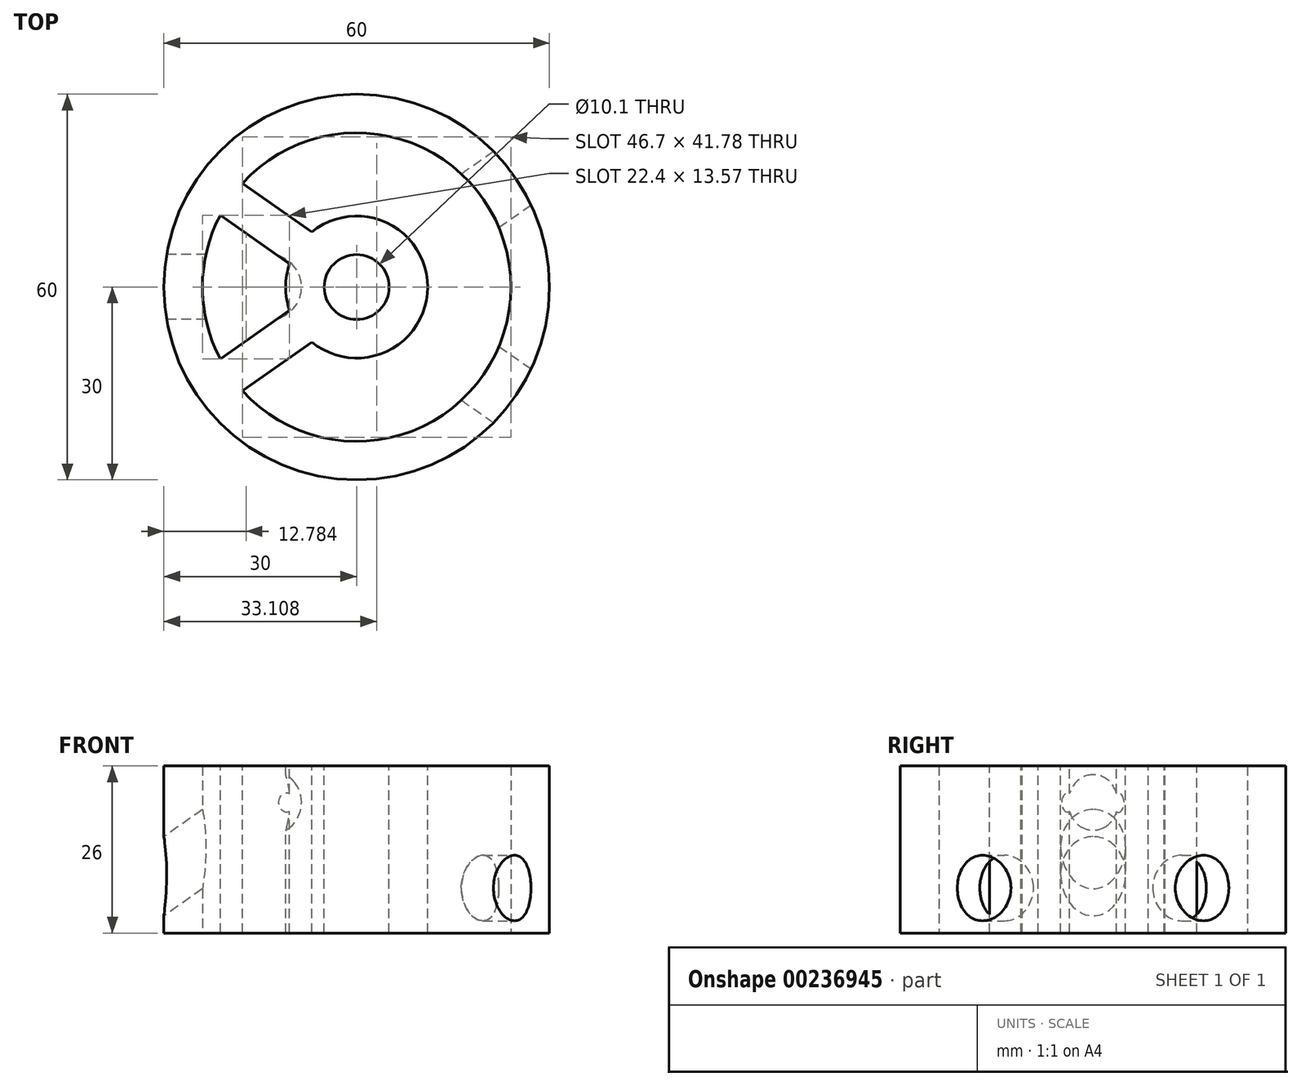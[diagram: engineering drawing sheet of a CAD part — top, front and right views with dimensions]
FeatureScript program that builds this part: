
annotation { "Feature Type Name" : "Feature", "Feature Type Description" : "" }
export const myFeature = defineFeature(function(context is Context, id is Id, definition is map)
    precondition{}
    {
        {
            var Q0;
            Q0=qCreatedBy(makeId("Top.planeOp"),FACE);
            var sketch = newSketch(context, id + "F0", { "sketchPlane" : qUnion([Q0])});
            skCircle(sketch, "E0", {"center": v(0, 0) * mm, "radius": 30 * mm});
            skCircle(sketch, "E1", {"center": v(0, 0) * mm, "radius": 24 * mm});
            skSolve(sketch);
        }
        {
            var Q0;
            Q0 = qSketchRegion(id + "F0", true);
            extrude(context, id + "F1", {"entities" : qUnion([Q0]), "depth" : 26 * mm});
        }
        {
            var Q0;
            Q0=makeQuery(id+"F1.opExtrude","CAP_FACE",FACE,{"disambiguationData":[OSD([sQuery(id+"F0.wireOp",EDGE,"E0"),sQuery(id+"F0.wireOp",EDGE,"E1")])],"isStart":false});
            var sketch = newSketch(context, id + "F2", { "sketchPlane" : qUnion([Q0])});
            skCircle(sketch, "E2", {"center": v(0, 0) * mm, "radius": 5.05 * mm});
            skCircle(sketch, "E3", {"center": v(0, 0) * mm, "radius": 11.05 * mm});
            skLineSegment(sketch, "E4", {"start": v(0, 0) * mm, "end": v(-19.66, 13.77) * mm});
            skLineSegment(sketch, "E5", {"start": v(0, 0) * mm, "end": v(-19.66, -13.77) * mm});
            skLineSegment(sketch, "E6", {"start": v(0, 0) * mm, "end": v(19.66, -13.77) * mm});
            skLineSegment(sketch, "E7", {"start": v(0, 0) * mm, "end": v(19.66, 13.77) * mm});
            skLineSegment(sketch, "E8.0", {"start": v(-1.72, 2.46) * mm, "end": v(-21.38, -11.3) * mm});
            skLineSegment(sketch, "E8.1", {"start": v(-1.72, 2.46) * mm, "end": v(17.94, 16.22) * mm});
            skLineSegment(sketch, "E9.0", {"start": v(1.72, -2.46) * mm, "end": v(-17.94, -16.22) * mm});
            skLineSegment(sketch, "E9.1", {"start": v(1.72, -2.46) * mm, "end": v(21.38, 11.3) * mm});
            skCircle(sketch, "E10", {"center": v(0, 0) * mm, "radius": 24 * mm});
            skLineSegment(sketch, "E11.0", {"start": v(1.72, 2.46) * mm, "end": v(-17.94, 16.22) * mm});
            skLineSegment(sketch, "E11.1", {"start": v(1.72, 2.46) * mm, "end": v(21.38, -11.3) * mm});
            skLineSegment(sketch, "E12.0", {"start": v(-1.72, -2.46) * mm, "end": v(-21.38, 11.3) * mm});
            skLineSegment(sketch, "E12.1", {"start": v(-1.72, -2.46) * mm, "end": v(17.94, -16.22) * mm});
            skSolve(sketch);
        }
        {
            var Q0;
            {var subQ0=sQuery(id+"F2.wireOp",EDGE,"E4");var subQ1=sQuery(id+"F2.wireOp",EDGE,"E3");var subQ2=makeQuery(id+"F2.imprint","INTERSECT",VERTEX,{"derivedFrom":[subQ1,subQ0]});Q0=makeQuery(id+"F2.imprint","IMPRINT",FACE,{"disambiguationData":[TD([[makeQuery(id+"F2.imprint","IMPRINT",EDGE,{"disambiguationData":[TD([[subQ2,-1.0]])],"derivedFrom":subQ1}),-1.0]])]});}
            var Q1;
            {var subQ0=sQuery(id+"F2.wireOp",EDGE,"E11.0");var subQ1=sQuery(id+"F2.wireOp",EDGE,"E3");var subQ2=makeQuery(id+"F2.imprint","INTERSECT",VERTEX,{"derivedFrom":[subQ1,subQ0]});Q1=makeQuery(id+"F2.imprint","IMPRINT",FACE,{"disambiguationData":[TD([[makeQuery(id+"F2.imprint","IMPRINT",EDGE,{"disambiguationData":[TD([[subQ2,-1.0]])],"derivedFrom":subQ1}),-1.0]])]});}
            var Q2;
            {var subQ0=sQuery(id+"F2.wireOp",EDGE,"E11.0");var subQ1=sQuery(id+"F2.wireOp",EDGE,"E2");var subQ2=makeQuery(id+"F2.imprint","INTERSECT",VERTEX,{"derivedFrom":[subQ1,subQ0]});Q2=makeQuery(id+"F2.imprint","IMPRINT",FACE,{"disambiguationData":[TD([[makeQuery(id+"F2.imprint","IMPRINT",EDGE,{"disambiguationData":[TD([[subQ2,-1.0]])],"derivedFrom":subQ1}),-1.0]])]});}
            var Q3;
            {var subQ0=sQuery(id+"F2.wireOp",EDGE,"E4");var subQ1=sQuery(id+"F2.wireOp",EDGE,"E2");var subQ2=makeQuery(id+"F2.imprint","INTERSECT",VERTEX,{"derivedFrom":[subQ1,subQ0]});Q3=makeQuery(id+"F2.imprint","IMPRINT",FACE,{"disambiguationData":[TD([[makeQuery(id+"F2.imprint","IMPRINT",EDGE,{"disambiguationData":[TD([[subQ2,-1.0]])],"derivedFrom":subQ1}),-1.0]])]});}
            var Q4;
            {var subQ0=sQuery(id+"F2.wireOp",EDGE,"E12.0");var subQ1=sQuery(id+"F2.wireOp",EDGE,"E3");var subQ2=makeQuery(id+"F2.imprint","INTERSECT",VERTEX,{"derivedFrom":[subQ1,subQ0]});Q4=makeQuery(id+"F2.imprint","IMPRINT",FACE,{"disambiguationData":[TD([[makeQuery(id+"F2.imprint","IMPRINT",EDGE,{"disambiguationData":[TD([[subQ2,-1.0]])],"derivedFrom":subQ1}),1.0]])]});}
            var Q5;
            {var subQ5=sQuery(id+"F2.wireOp",EDGE,"E12.0");var subQ6=sQuery(id+"F2.wireOp",EDGE,"E2");var subQ7=makeQuery(id+"F2.imprint","INTERSECT",VERTEX,{"derivedFrom":[subQ6,subQ5]});Q5=makeQuery(id+"F2.imprint","IMPRINT",FACE,{"disambiguationData":[TD([[makeQuery(id+"F2.imprint","IMPRINT",EDGE,{"disambiguationData":[TD([[subQ7,-1.0]])],"derivedFrom":subQ6}),-1.0]])]});}
            var Q6;
            {var subQ0=sQuery(id+"F2.wireOp",EDGE,"E5");var subQ1=sQuery(id+"F2.wireOp",EDGE,"E2");var subQ2=makeQuery(id+"F2.imprint","INTERSECT",VERTEX,{"derivedFrom":[subQ1,subQ0]});Q6=makeQuery(id+"F2.imprint","IMPRINT",FACE,{"disambiguationData":[TD([[makeQuery(id+"F2.imprint","IMPRINT",EDGE,{"disambiguationData":[TD([[subQ2,-1.0]])],"derivedFrom":subQ1}),-1.0]])]});}
            var Q7;
            {var subQ0=sQuery(id+"F2.wireOp",EDGE,"E9.0");var subQ1=sQuery(id+"F2.wireOp",EDGE,"E2");var subQ2=makeQuery(id+"F2.imprint","INTERSECT",VERTEX,{"derivedFrom":[subQ1,subQ0]});Q7=makeQuery(id+"F2.imprint","IMPRINT",FACE,{"disambiguationData":[TD([[makeQuery(id+"F2.imprint","IMPRINT",EDGE,{"disambiguationData":[TD([[subQ2,-1.0]])],"derivedFrom":subQ1}),-1.0]])]});}
            var Q8;
            {var subQ0=sQuery(id+"F2.wireOp",EDGE,"E12.1");var subQ1=sQuery(id+"F2.wireOp",EDGE,"E2");var subQ2=makeQuery(id+"F2.imprint","INTERSECT",VERTEX,{"derivedFrom":[subQ1,subQ0]});Q8=makeQuery(id+"F2.imprint","IMPRINT",FACE,{"disambiguationData":[TD([[makeQuery(id+"F2.imprint","IMPRINT",EDGE,{"disambiguationData":[TD([[subQ2,-1.0]])],"derivedFrom":subQ1}),-1.0]])]});}
            var Q9;
            {var subQ1=sQuery(id+"F2.wireOp",EDGE,"E2");var subQ5=sQuery(id+"F2.wireOp",EDGE,"E6");var subQ6=makeQuery(id+"F2.imprint","INTERSECT",VERTEX,{"derivedFrom":[subQ1,subQ5]});Q9=makeQuery(id+"F2.imprint","IMPRINT",FACE,{"disambiguationData":[TD([[makeQuery(id+"F2.imprint","IMPRINT",EDGE,{"disambiguationData":[TD([[subQ6,-1.0]])],"derivedFrom":subQ1}),-1.0]])]});}
            var Q10;
            {var subQ0=sQuery(id+"F2.wireOp",EDGE,"E9.1");var subQ1=sQuery(id+"F2.wireOp",EDGE,"E3");var subQ2=makeQuery(id+"F2.imprint","INTERSECT",VERTEX,{"derivedFrom":[subQ1,subQ0]});Q10=makeQuery(id+"F2.imprint","IMPRINT",FACE,{"disambiguationData":[TD([[makeQuery(id+"F2.imprint","IMPRINT",EDGE,{"disambiguationData":[TD([[subQ2,1.0]])],"derivedFrom":subQ1}),1.0]])]});}
            var Q11;
            {var subQ0=sQuery(id+"F2.wireOp",EDGE,"E7");var subQ1=sQuery(id+"F2.wireOp",EDGE,"E2");var subQ2=makeQuery(id+"F2.imprint","INTERSECT",VERTEX,{"derivedFrom":[subQ1,subQ0]});Q11=makeQuery(id+"F2.imprint","IMPRINT",FACE,{"disambiguationData":[TD([[makeQuery(id+"F2.imprint","IMPRINT",EDGE,{"disambiguationData":[TD([[subQ2,1.0]])],"derivedFrom":subQ1}),-1.0]])]});}
            var Q12;
            {var subQ0=sQuery(id+"F2.wireOp",EDGE,"E7");var subQ1=sQuery(id+"F2.wireOp",EDGE,"E2");var subQ2=makeQuery(id+"F2.imprint","INTERSECT",VERTEX,{"derivedFrom":[subQ1,subQ0]});Q12=makeQuery(id+"F2.imprint","IMPRINT",FACE,{"disambiguationData":[TD([[makeQuery(id+"F2.imprint","IMPRINT",EDGE,{"disambiguationData":[TD([[subQ2,-1.0]])],"derivedFrom":subQ1}),-1.0]])]});}
            var Q13;
            {var subQ0=sQuery(id+"F2.wireOp",EDGE,"E8.1");var subQ1=sQuery(id+"F2.wireOp",EDGE,"E2");var subQ2=makeQuery(id+"F2.imprint","INTERSECT",VERTEX,{"derivedFrom":[subQ1,subQ0]});Q13=makeQuery(id+"F2.imprint","IMPRINT",FACE,{"disambiguationData":[TD([[makeQuery(id+"F2.imprint","IMPRINT",EDGE,{"disambiguationData":[TD([[subQ2,-1.0]])],"derivedFrom":subQ1}),-1.0]])]});}
            var Q14;
            {var subQ0=sQuery(id+"F2.wireOp",EDGE,"E8.0");var subQ1=sQuery(id+"F2.wireOp",EDGE,"E2");var subQ2=makeQuery(id+"F2.imprint","INTERSECT",VERTEX,{"derivedFrom":[subQ1,subQ0]});Q14=makeQuery(id+"F2.imprint","IMPRINT",FACE,{"disambiguationData":[TD([[makeQuery(id+"F2.imprint","IMPRINT",EDGE,{"disambiguationData":[TD([[subQ2,-1.0]])],"derivedFrom":subQ1}),-1.0]])]});}
            var Q15;
            {var subQ0=sQuery(id+"F2.wireOp",EDGE,"E11.1");var subQ1=sQuery(id+"F2.wireOp",EDGE,"E2");var subQ2=makeQuery(id+"F2.imprint","INTERSECT",VERTEX,{"derivedFrom":[subQ1,subQ0]});Q15=makeQuery(id+"F2.imprint","IMPRINT",FACE,{"disambiguationData":[TD([[makeQuery(id+"F2.imprint","IMPRINT",EDGE,{"disambiguationData":[TD([[subQ2,1.0]])],"derivedFrom":subQ1}),-1.0]])]});}
            var Q16;
            {var subQ0=sQuery(id+"F2.wireOp",EDGE,"E8.0");var subQ1=sQuery(id+"F2.wireOp",EDGE,"E3");var subQ2=makeQuery(id+"F2.imprint","INTERSECT",VERTEX,{"derivedFrom":[subQ1,subQ0]});Q16=makeQuery(id+"F2.imprint","IMPRINT",FACE,{"disambiguationData":[TD([[makeQuery(id+"F2.imprint","IMPRINT",EDGE,{"disambiguationData":[TD([[subQ2,-1.0]])],"derivedFrom":subQ1}),-1.0]])]});}
            var Q17;
            {var subQ0=sQuery(id+"F2.wireOp",EDGE,"E5");var subQ1=sQuery(id+"F2.wireOp",EDGE,"E3");var subQ2=makeQuery(id+"F2.imprint","INTERSECT",VERTEX,{"derivedFrom":[subQ1,subQ0]});Q17=makeQuery(id+"F2.imprint","IMPRINT",FACE,{"disambiguationData":[TD([[makeQuery(id+"F2.imprint","IMPRINT",EDGE,{"disambiguationData":[TD([[subQ2,-1.0]])],"derivedFrom":subQ1}),-1.0]])]});}
            extrude(context, id + "F3", {"entities" : qUnion([Q0, Q1, Q2, Q3, Q4, Q5, Q6, Q7, Q8, Q9, Q10, Q11, Q12, Q13, Q14, Q15, Q16, Q17]), "operationType" : NewBodyOperationType.ADD, "oppositeDirection" : true, "depth" : 26 * mm});
        }
        {
            var Q0;
            Q0=qCreatedBy(makeId("Front.planeOp"),FACE);
            var sketch = newSketch(context, id + "F4", { "sketchPlane" : qUnion([Q0])});
            skLineSegment(sketch, "E13", {"start": v(-30, 0) * mm, "end": v(-30, 28) * mm});
            skLineSegment(sketch, "E14", {"start": v(30, 28) * mm, "end": v(30, 0) * mm});
            skLineSegment(sketch, "E15.0", {"start": v(-30, 0) * mm, "end": v(30, 0) * mm});
            skLineSegment(sketch, "E16", {"start": v(-30, 15) * mm, "end": v(-16.52, 24.44) * mm});
            skLineSegment(sketch, "E17", {"start": v(-9.5, 23.2) * mm, "end": v(-9.5, 23.2) * mm});
            skLineSegment(sketch, "E18", {"start": v(-10.73, 16.16) * mm, "end": v(-35.94, -1.5) * mm});
            skLineSegment(sketch, "E19", {"start": v(-35.94, -1.5) * mm, "end": v(-41.73, 6.78) * mm});
            skLineSegment(sketch, "E20", {"start": v(-30, 15) * mm, "end": v(-41.73, 6.78) * mm});
            skPoint(sketch, "E21.visualSharp", {"position": v(-6.6, 19.06) * mm});
            skArc(sketch, "E21.filletArc", {"start": v(-10.73, 16.16) * mm, "mid": v(-8.66, 19.42) * mm, "end": v(-9.5, 23.2) * mm});
            skPoint(sketch, "E22.visualSharp", {"position": v(-12.39, 27.33) * mm});
            skArc(sketch, "E22.filletArc", {"start": v(-9.5, 23.2) * mm, "mid": v(-12.75, 25.27) * mm, "end": v(-16.52, 24.44) * mm});
            skLineSegment(sketch, "E23", {"start": v(-9.5, 23.2) * mm, "end": v(-38.84, 2.65) * mm});
            skSolve(sketch);
        }
        {
            var Q0;
            {var subQ0=sQuery(id+"F4.wireOp",EDGE,"E16");Q0=makeQuery(id+"F4.imprint","IMPRINT",FACE,{"disambiguationData":[TD([[makeQuery(id+"F4.imprint","IMPRINT",EDGE,{"derivedFrom":subQ0}),-1.0]])]});}
            var Q1;
            {var subQ0=sQuery(id+"F4.wireOp",EDGE,"E20");Q1=makeQuery(id+"F4.imprint","IMPRINT",FACE,{"disambiguationData":[TD([[makeQuery(id+"F4.imprint","IMPRINT",EDGE,{"derivedFrom":subQ0}),1.0]])]});}
            var Q2;
            Q2=sQuery(id+"F4.wireOp",EDGE,"E23");
            revolve(context, id + "F5", {"operationType" : NewBodyOperationType.REMOVE, "entities" : qUnion([Q0, Q1]), "axis" : qUnion([Q2]), "revolveType" : RevolveType.FULL, "oppositeDirection" : true});
        }
        {
            var Q0;
            Q0=makeQuery(id+"F3.boolean.opBoolean","MERGE",FACE,{"derivedFrom":[makeQuery(id+"F1.opExtrude","CAP_FACE",FACE,{"disambiguationData":[OSD([sQuery(id+"F0.wireOp",EDGE,"E0"),sQuery(id+"F0.wireOp",EDGE,"E1")])],"isStart":false}),makeQuery(id+"F3.opExtrude","CAP_FACE",FACE,{"disambiguationData":[OSD([sQuery(id+"F2.wireOp",EDGE,"E2"),sQuery(id+"F2.wireOp",EDGE,"E3"),sQuery(id+"F2.wireOp",EDGE,"E8.0"),sQuery(id+"F2.wireOp",EDGE,"E9.0"),sQuery(id+"F2.wireOp",EDGE,"E10"),sQuery(id+"F2.wireOp",EDGE,"E11.0"),sQuery(id+"F2.wireOp",EDGE,"E12.0")])],"isStart":true})]});
            var sketch = newSketch(context, id + "F6", { "sketchPlane" : qUnion([Q0])});
            skLineSegment(sketch, "E24", {"start": v(0, 0) * mm, "end": v(24.57, 17.2) * mm});
            skLineSegment(sketch, "E25", {"start": v(0, 0) * mm, "end": v(24.57, -17.2) * mm});
            skLineSegment(sketch, "E26.0", {"start": v(2.93, -4.18) * mm, "end": v(27.5, 13.03) * mm});
            skLineSegment(sketch, "E27.0", {"start": v(-2.93, 4.18) * mm, "end": v(21.65, 21.38) * mm});
            skLineSegment(sketch, "E28.0", {"start": v(-2.93, -4.18) * mm, "end": v(21.65, -21.38) * mm});
            skLineSegment(sketch, "E29.0", {"start": v(2.93, 4.18) * mm, "end": v(27.5, -13.03) * mm});
            skCircle(sketch, "E30", {"center": v(0, 0) * mm, "radius": 30 * mm});
            skSolve(sketch);
        }
        {
            var Q0;
            {var subQ0=sQuery(id+"F6.wireOp",EDGE,"E30");var subQ1=sQuery(id+"F6.wireOp",EDGE,"E24");var subQ2=makeQuery(id+"F6.imprint","INTERSECT",VERTEX,{"derivedFrom":[subQ1,subQ0]});Q0=makeQuery(id+"F6.imprint","IMPRINT",FACE,{"disambiguationData":[TD([[makeQuery(id+"F6.imprint","IMPRINT",EDGE,{"disambiguationData":[TD([[subQ2,-1.0]])],"derivedFrom":subQ0}),1.0]])]});}
            var Q1;
            {var subQ0=sQuery(id+"F6.wireOp",EDGE,"E30");var subQ1=sQuery(id+"F6.wireOp",EDGE,"E24");var subQ2=makeQuery(id+"F6.imprint","INTERSECT",VERTEX,{"derivedFrom":[subQ1,subQ0]});Q1=makeQuery(id+"F6.imprint","IMPRINT",FACE,{"disambiguationData":[TD([[makeQuery(id+"F6.imprint","IMPRINT",EDGE,{"disambiguationData":[TD([[subQ2,1.0]])],"derivedFrom":subQ0}),1.0]])]});}
            var Q2;
            {var subQ0=sQuery(id+"F6.wireOp",EDGE,"E30");var subQ1=sQuery(id+"F6.wireOp",EDGE,"E25");var subQ2=makeQuery(id+"F6.imprint","INTERSECT",VERTEX,{"derivedFrom":[subQ1,subQ0]});Q2=makeQuery(id+"F6.imprint","IMPRINT",FACE,{"disambiguationData":[TD([[makeQuery(id+"F6.imprint","IMPRINT",EDGE,{"disambiguationData":[TD([[subQ2,-1.0]])],"derivedFrom":subQ0}),1.0]])]});}
            var Q3;
            {var subQ0=sQuery(id+"F6.wireOp",EDGE,"E30");var subQ1=sQuery(id+"F6.wireOp",EDGE,"E25");var subQ2=makeQuery(id+"F6.imprint","INTERSECT",VERTEX,{"derivedFrom":[subQ1,subQ0]});Q3=makeQuery(id+"F6.imprint","IMPRINT",FACE,{"disambiguationData":[TD([[makeQuery(id+"F6.imprint","IMPRINT",EDGE,{"disambiguationData":[TD([[subQ2,1.0]])],"derivedFrom":subQ0}),1.0]])]});}
            extrude(context, id + "F7", {"entities" : qUnion([Q0, Q1, Q2, Q3]), "operationType" : NewBodyOperationType.REMOVE, "oppositeDirection" : true, "depth" : (26 - 1.9) * mm, "hasSecondDirection" : true, "secondDirectionOppositeDirection" : true, "secondDirectionDepth" : (24.1 - 10.2) * mm});
        }
        {
            var Q0;
            Q0=makeQuery(id+"F7.boolean.opBoolean","COPY",EDGE,{"derivedFrom":makeQuery(id+"F7.opExtrude","CAP_EDGE",EDGE,{"disambiguationData":[OSD([sQuery(id+"F6.wireOp",EDGE,"E28.0")])],"isStart":false})});
            var Q1;
            Q1=makeQuery(id+"F7.boolean.opBoolean","COPY",EDGE,{"derivedFrom":makeQuery(id+"F7.opExtrude","CAP_EDGE",EDGE,{"disambiguationData":[OSD([sQuery(id+"F6.wireOp",EDGE,"E28.0")])],"isStart":true})});
            var Q2;
            Q2=makeQuery(id+"F7.boolean.opBoolean","COPY",EDGE,{"derivedFrom":makeQuery(id+"F7.opExtrude","CAP_EDGE",EDGE,{"disambiguationData":[OSD([sQuery(id+"F6.wireOp",EDGE,"E29.0")])],"isStart":true})});
            var Q3;
            Q3=makeQuery(id+"F7.boolean.opBoolean","COPY",EDGE,{"derivedFrom":makeQuery(id+"F7.opExtrude","CAP_EDGE",EDGE,{"disambiguationData":[OSD([sQuery(id+"F6.wireOp",EDGE,"E29.0")])],"isStart":false})});
            var Q4;
            Q4=makeQuery(id+"F7.boolean.opBoolean","COPY",EDGE,{"derivedFrom":makeQuery(id+"F7.opExtrude","CAP_EDGE",EDGE,{"disambiguationData":[OSD([sQuery(id+"F6.wireOp",EDGE,"E27.0")])],"isStart":false})});
            var Q5;
            Q5=makeQuery(id+"F7.boolean.opBoolean","COPY",EDGE,{"derivedFrom":makeQuery(id+"F7.opExtrude","CAP_EDGE",EDGE,{"disambiguationData":[OSD([sQuery(id+"F6.wireOp",EDGE,"E27.0")])],"isStart":true})});
            var Q6;
            Q6=makeQuery(id+"F7.boolean.opBoolean","COPY",EDGE,{"derivedFrom":makeQuery(id+"F7.opExtrude","CAP_EDGE",EDGE,{"disambiguationData":[OSD([sQuery(id+"F6.wireOp",EDGE,"E26.0")])],"isStart":true})});
            var Q7;
            Q7=makeQuery(id+"F7.boolean.opBoolean","COPY",EDGE,{"derivedFrom":makeQuery(id+"F7.opExtrude","CAP_EDGE",EDGE,{"disambiguationData":[OSD([sQuery(id+"F6.wireOp",EDGE,"E26.0")])],"isStart":false})});
            fillet(context, id + "F8", {"entities" : qUnion([Q0, Q1, Q2, Q3, Q4, Q5, Q6, Q7]), "radius" : 5.1 * mm, "tangentPropagation" : true, "allowEdgeOverflow" : false});
        }
    });
